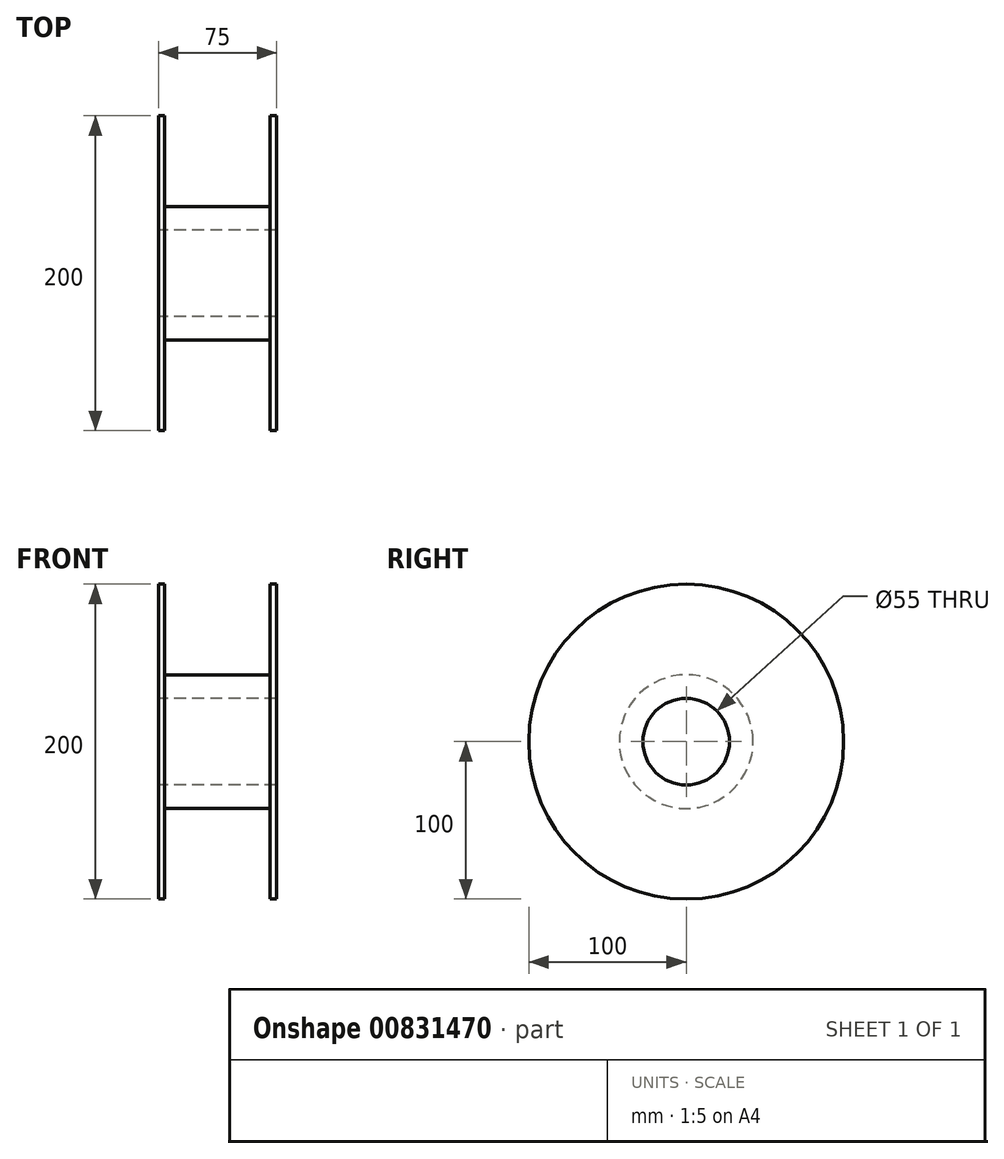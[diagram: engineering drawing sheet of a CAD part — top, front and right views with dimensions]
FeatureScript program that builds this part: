
annotation { "Feature Type Name" : "Feature", "Feature Type Description" : "" }
export const myFeature = defineFeature(function(context is Context, id is Id, definition is map)
    precondition{}
    {
        {
            var Q0;
            Q0=qCreatedBy(makeId("Right.planeOp"),FACE);
            var sketch = newSketch(context, id + "F0", { "sketchPlane" : qUnion([Q0])});
            skCircle(sketch, "E0", {"center": v(0, 0) * mm, "radius": 42.5 * mm});
            skCircle(sketch, "E1", {"center": v(0, 0) * mm, "radius": 27.5 * mm});
            skSolve(sketch);
        }
        {
            var Q0;
            Q0=makeQuery(id+"F0.imprint","IMPRINT",FACE,{"disambiguationData":[TD([[makeQuery(id+"F0.imprint","IMPRINT",EDGE,{"derivedFrom":sQuery(id+"F0.wireOp",EDGE,"E0")}),1.0]])]});
            extrude(context, id + "F1", {"entities" : qUnion([Q0]), "endBound" : BoundingType.SYMMETRIC, "depth" : 67 * mm, "offsetDistance" : 25 * mm});
        }
        {
            var Q0;
            Q0=makeQuery(id+"F1.opExtrude","CAP_FACE",FACE,{"disambiguationData":[OSD([sQuery(id+"F0.wireOp",EDGE,"E0"),sQuery(id+"F0.wireOp",EDGE,"E1")])],"isStart":false});
            var sketch = newSketch(context, id + "F2", { "sketchPlane" : qUnion([Q0])});
            skCircle(sketch, "E2", {"center": v(0, 0) * mm, "radius": 100 * mm});
            skSolve(sketch);
        }
        {
            var Q0;
            Q0=makeQuery(id+"F2.imprint","IMPRINT",FACE,{"disambiguationData":[TD([[makeQuery(id+"F2.imprint","IMPRINT",EDGE,{"derivedFrom":sQuery(id+"F2.wireOp",EDGE,"E2")}),1.0]])]});
            var Q1;
            Q1=makeQuery(id+"F2.imprint","IMPRINT",FACE,{"disambiguationData":[TD([[makeQuery(id+"F2.imprint","IMPRINT",EDGE,{"derivedFrom":makeQuery(id+"F1.opExtrude","CAP_EDGE",EDGE,{"disambiguationData":[OSD([sQuery(id+"F0.wireOp",EDGE,"E0")])],"isStart":false})}),1.0]])]});
            extrude(context, id + "F3", {"entities" : qUnion([Q0, Q1]), "operationType" : NewBodyOperationType.ADD, "depth" : 4 * mm, "offsetDistance" : 25 * mm});
        }
        {
            var Q0;
            Q0=makeQuery(id+"F1.opExtrude","CAP_FACE",FACE,{"disambiguationData":[OSD([sQuery(id+"F0.wireOp",EDGE,"E0"),sQuery(id+"F0.wireOp",EDGE,"E1")])],"isStart":true});
            var sketch = newSketch(context, id + "F4", { "sketchPlane" : qUnion([Q0])});
            skCircle(sketch, "E3", {"center": v(0, 0) * mm, "radius": 100 * mm});
            skSolve(sketch);
        }
        {
            var Q0;
            Q0=makeQuery(id+"F4.imprint","IMPRINT",FACE,{"disambiguationData":[TD([[makeQuery(id+"F4.imprint","IMPRINT",EDGE,{"derivedFrom":sQuery(id+"F4.wireOp",EDGE,"F8qICgZH-YWy1-PGZB-caCI-pqj53DjCW0xo")}),1.0]])]});
            var Q1;
            Q1=makeQuery(id+"F4.imprint","IMPRINT",FACE,{"disambiguationData":[TD([[makeQuery(id+"F4.imprint","IMPRINT",EDGE,{"derivedFrom":makeQuery(id+"F1.opExtrude","CAP_EDGE",EDGE,{"disambiguationData":[OSD([sQuery(id+"F0.wireOp",EDGE,"E0")])],"isStart":true})}),-1.0]])]});
            var Q2;
            Q2=makeQuery(id+"F4.imprint","IMPRINT",FACE,{"disambiguationData":[TD([[makeQuery(id+"F4.imprint","IMPRINT",EDGE,{"derivedFrom":sQuery(id+"F4.wireOp",EDGE,"E3")}),1.0]])]});
            extrude(context, id + "F5", {"entities" : qUnion([Q0, Q1, Q2]), "operationType" : NewBodyOperationType.ADD, "depth" : 4 * mm, "offsetDistance" : 25 * mm});
        }
    });
